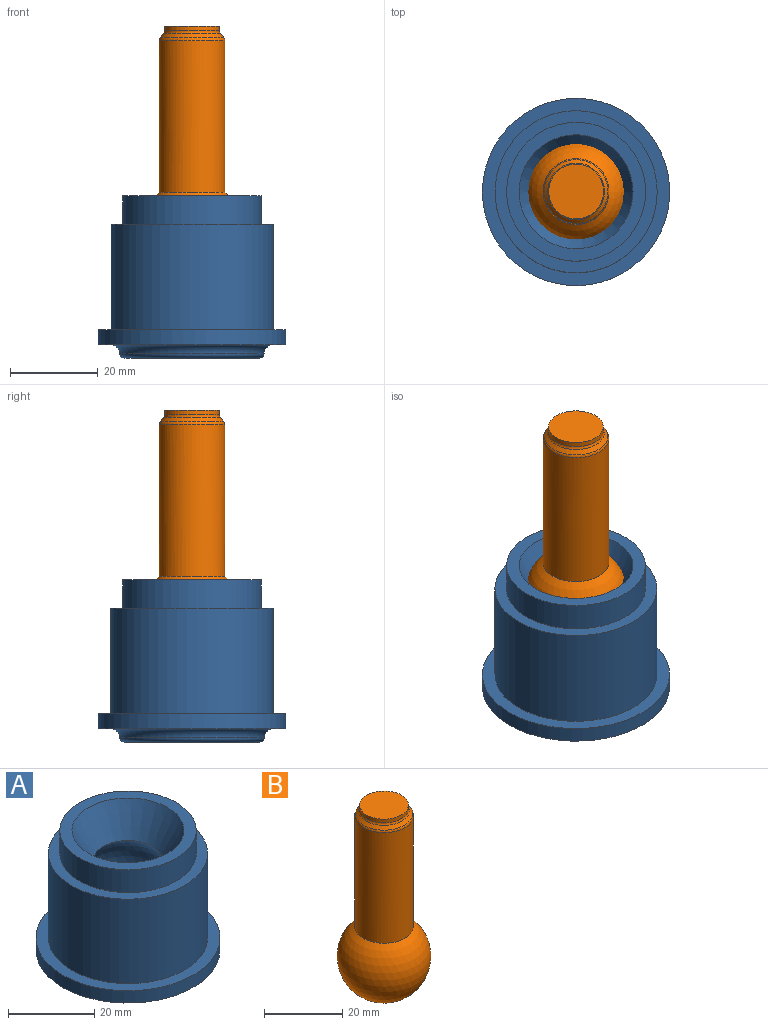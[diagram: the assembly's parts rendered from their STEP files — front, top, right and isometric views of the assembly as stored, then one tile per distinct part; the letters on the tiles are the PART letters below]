
ASSEMBLY  parts=2 mates=1
PART A: 15 faces, bbox 43.1x43.1x37.7 mm
  f0: cylinder r=18.5mm len=37mm, axis (0,0,-1), area 2789.7mm2, adj f1,f8
  f1: plane 37x37mm, normal (0,0,1), area 286mm2, adj f0,f2
  f2: cylinder r=15.85mm len=31.7mm, axis (0,0,-1), area 647.3mm2, adj f1,f3
  f3: plane 31.7x31.7mm, normal (0,0,1), area 258.3mm2, adj f2,f5
  f4: sphere r=12mm, area 1576.3mm2, adj f5
  f5: cone r=13mm half-angle=30deg, axis (0,0,1), area 655.5mm2, adj f3,f4
  f6: cylinder r=21.38mm len=42.75mm, axis (0,0,1), area 470.1mm2, adj f7,f8
  f7: plane 42.75x42.75mm, normal (0,0,-1), area 360.2mm2, adj f6,f10
  f8: plane 42.75x42.75mm, normal (0,0,1), area 360.2mm2, adj f0,f6
  f9: plane 31x31mm, normal (0,0,-1), area 173.8mm2, adj f11,f14
  f10: torus R=18.5mm, axis (0,0,-1), area 340mm2, adj f7,f11
  f11: torus R=15.5mm, axis (0,0,-1), area 159.3mm2, adj f9,f10
  f12: plane 22.25x22.25mm, normal (0,0,-1), area 388.9mm2, adj f13
  f13: torus R=11.13mm, axis (0,0,1), area 146.3mm2, adj f12,f14
  f14: torus R=13.6mm, axis (0,0,-1), area 80mm2, adj f9,f13
PART B: 7 faces, bbox 24x24x59.4 mm
  f0: plane 12.5x12.5mm, normal (0,0,1), area 122.7mm2, adj f4
  f1: sphere r=12mm, area 1611.1mm2, adj f2
  f2: cylinder r=7.5mm len=34.64mm, axis (0,0,1), area 1632.3mm2, adj f1,f5
  f3: cone r=6.25mm half-angle=39.8deg, axis (0,0,-1), area 53.1mm2, adj f5,f6
  f4: cylinder r=6.25mm len=12.5mm, axis (0,0,1), area 44.7mm2, adj f0,f6
  f5: torus R=6.5mm, axis (0,0,-1), area 32.4mm2, adj f2,f3
  f6: torus R=7.25mm, axis (0,0,1), area 27.6mm2, adj f3,f4
PLACE A at identity
PLACE B t=(0,0,21.91)mm
MATE ball B.f6 <-> A.f5  axis (0,0,1) through (0,0,21.91)mm
